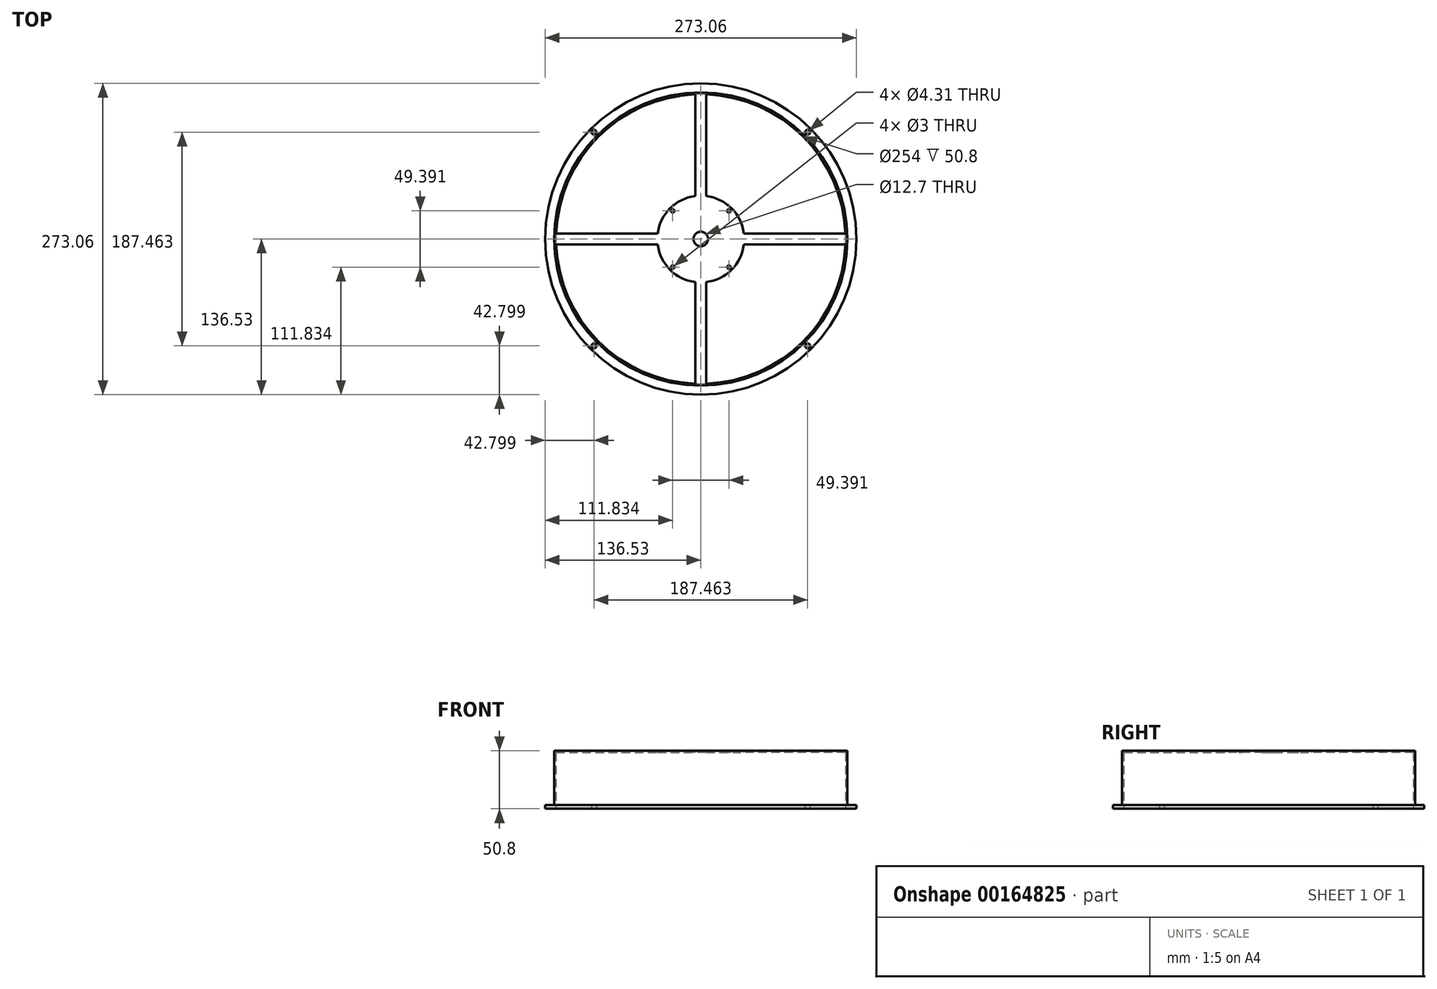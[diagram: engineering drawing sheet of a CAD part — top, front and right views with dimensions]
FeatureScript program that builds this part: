
annotation { "Feature Type Name" : "Feature", "Feature Type Description" : "" }
export const myFeature = defineFeature(function(context is Context, id is Id, definition is map)
    precondition{}
    {
        {
            var Q0;
            Q0=qCreatedBy(makeId("Top.planeOp"),FACE);
            var sketch = newSketch(context, id + "F0", { "sketchPlane" : qUnion([Q0])});
            skCircle(sketch, "E0", {"center": v(0, 0) * mm, "radius": 136.53 * mm});
            skLineSegment(sketch, "E1.bottom", {"start": v(93.73, 93.73) * mm, "end": v(-93.73, 93.73) * mm, "construction": true});
            skLineSegment(sketch, "E1.top", {"start": v(93.73, -93.73) * mm, "end": v(-93.73, -93.73) * mm, "construction": true});
            skLineSegment(sketch, "E1.left", {"start": v(93.73, 93.73) * mm, "end": v(93.73, -93.73) * mm, "construction": true});
            skLineSegment(sketch, "E1.right", {"start": v(-93.73, 93.73) * mm, "end": v(-93.73, -93.73) * mm, "construction": true});
            skCircle(sketch, "E2", {"center": v(93.73, 93.73) * mm, "radius": 3.97 * mm, "construction": true});
            skCircle(sketch, "E3", {"center": v(-93.73, 93.73) * mm, "radius": 2.15 * mm});
            skCircle(sketch, "E4", {"center": v(93.73, 93.73) * mm, "radius": 2.15 * mm});
            skCircle(sketch, "E5", {"center": v(93.73, -93.73) * mm, "radius": 2.15 * mm});
            skCircle(sketch, "E6", {"center": v(-93.73, -93.73) * mm, "radius": 2.15 * mm});
            skCircle(sketch, "E7", {"center": v(0, 0) * mm, "radius": 127 * mm});
            skSolve(sketch);
        }
        {
            var Q0;
            Q0 = qSketchRegion(id + "F0", true);
            extrude(context, id + "F1", {"entities" : qUnion([Q0]), "depth" : 3.17 * mm});
        }
        {
            var Q0;
            Q0=makeQuery(id+"F1.opExtrude","CAP_FACE",FACE,{"disambiguationData":[OSD([sQuery(id+"F0.wireOp",EDGE,"E0"),sQuery(id+"F0.wireOp",EDGE,"E3"),sQuery(id+"F0.wireOp",EDGE,"E4"),sQuery(id+"F0.wireOp",EDGE,"E5"),sQuery(id+"F0.wireOp",EDGE,"E6"),sQuery(id+"F0.wireOp",EDGE,"E7")])],"isStart":false});
            var sketch = newSketch(context, id + "F2", { "sketchPlane" : qUnion([Q0])});
            skCircle(sketch, "E8", {"center": v(0, 0) * mm, "radius": 127 * mm});
            skCircle(sketch, "E9", {"center": v(0, 0) * mm, "radius": 128.59 * mm});
            skSolve(sketch);
        }
        {
            var Q0;
            Q0 = qSketchRegion(id + "F2", true);
            extrude(context, id + "F3", {"entities" : qUnion([Q0]), "operationType" : NewBodyOperationType.ADD, "depth" : 47.62 * mm});
        }
        {
            var Q0;
            Q0=makeQuery(id+"F3.opExtrude","CAP_FACE",FACE,{"disambiguationData":[OSD([sQuery(id+"F2.wireOp",EDGE,"E8"),sQuery(id+"F2.wireOp",EDGE,"E9")])],"isStart":false});
            var sketch = newSketch(context, id + "F4", { "sketchPlane" : qUnion([Q0])});
            skLineSegment(sketch, "E10.bottom", {"start": v(-126.91, 4.76) * mm, "end": v(-37.8, 4.76) * mm});
            skLineSegment(sketch, "E10.top", {"start": v(-126.91, -4.76) * mm, "end": v(-37.8, -4.76) * mm});
            skLineSegment(sketch, "E10.left", {"start": v(-126.91, 4.76) * mm, "end": v(-126.91, -4.76) * mm, "construction": true});
            skLineSegment(sketch, "E10.right", {"start": v(-37.8, 4.76) * mm, "end": v(-37.8, -4.76) * mm});
            skLineSegment(sketch, "E11.bottom", {"start": v(126.91, -4.76) * mm, "end": v(37.8, -4.76) * mm});
            skLineSegment(sketch, "E11.top", {"start": v(126.91, 4.76) * mm, "end": v(37.8, 4.76) * mm});
            skLineSegment(sketch, "E11.left", {"start": v(126.91, -4.76) * mm, "end": v(126.91, 4.76) * mm, "construction": true});
            skLineSegment(sketch, "E11.right", {"start": v(37.8, -4.76) * mm, "end": v(37.8, 4.76) * mm});
            skLineSegment(sketch, "E12.bottom", {"start": v(-4.76, -126.91) * mm, "end": v(4.76, -126.91) * mm, "construction": true});
            skLineSegment(sketch, "E12.top", {"start": v(-4.76, -37.8) * mm, "end": v(4.76, -37.8) * mm});
            skLineSegment(sketch, "E12.left", {"start": v(-4.76, -126.91) * mm, "end": v(-4.76, -37.8) * mm});
            skLineSegment(sketch, "E12.right", {"start": v(4.76, -126.91) * mm, "end": v(4.76, -37.8) * mm});
            skLineSegment(sketch, "E13.bottom", {"start": v(-4.76, 126.91) * mm, "end": v(4.76, 126.91) * mm, "construction": true});
            skLineSegment(sketch, "E13.top", {"start": v(-4.76, 37.8) * mm, "end": v(4.76, 37.8) * mm});
            skLineSegment(sketch, "E13.left", {"start": v(-4.76, 126.91) * mm, "end": v(-4.76, 37.8) * mm});
            skLineSegment(sketch, "E13.right", {"start": v(4.76, 126.91) * mm, "end": v(4.76, 37.8) * mm});
            skLineSegment(sketch, "E14", {"start": v(0, 37.8) * mm, "end": v(0, -37.8) * mm, "construction": true});
            skArc(sketch, "E15", {"start": v(-37.8, -4.76) * mm, "mid": v(-26.94, -26.94) * mm, "end": v(-4.76, -37.8) * mm});
            skLineSegment(sketch, "E16", {"start": v(-37.8, 0) * mm, "end": v(37.8, 0) * mm, "construction": true});
            skArc(sketch, "E17", {"start": v(-4.76, 37.8) * mm, "mid": v(-26.94, 26.94) * mm, "end": v(-37.8, 4.76) * mm});
            skArc(sketch, "E18", {"start": v(37.8, 4.76) * mm, "mid": v(26.94, 26.94) * mm, "end": v(4.76, 37.8) * mm});
            skArc(sketch, "E19", {"start": v(4.76, -37.8) * mm, "mid": v(26.94, -26.94) * mm, "end": v(37.8, -4.76) * mm});
            skArc(sketch, "E20", {"start": v(4.76, 126.91) * mm, "mid": v(0, 127) * mm, "end": v(-4.76, 126.91) * mm});
            skCircle(sketch, "E21", {"center": v(0, 0) * mm, "radius": 127 * mm});
            skSolve(sketch);
        }
        {
            var Q0;
            {var subQ0=sQuery(id+"F4.wireOp",EDGE,"E10.bottom");Q0=makeQuery(id+"F4.imprint","IMPRINT",FACE,{"disambiguationData":[TD([[makeQuery(id+"F4.imprint","IMPRINT",EDGE,{"derivedFrom":subQ0}),-1.0]])]});}
            var Q1;
            {var subQ0=sQuery(id+"F4.wireOp",EDGE,"E11.bottom");Q1=makeQuery(id+"F4.imprint","IMPRINT",FACE,{"disambiguationData":[TD([[makeQuery(id+"F4.imprint","IMPRINT",EDGE,{"derivedFrom":subQ0}),-1.0]])]});}
            var Q2;
            Q2=makeQuery(id+"F4.imprint","IMPRINT",FACE,{"disambiguationData":[TD([[makeQuery(id+"F4.imprint","IMPRINT",EDGE,{"derivedFrom":sQuery(id+"F4.wireOp",EDGE,"E12.top")}),-1.0]])]});
            var Q3;
            Q3=makeQuery(id+"F4.imprint","IMPRINT",FACE,{"disambiguationData":[TD([[makeQuery(id+"F4.imprint","IMPRINT",EDGE,{"derivedFrom":sQuery(id+"F4.wireOp",EDGE,"E13.top")}),1.0]])]});
            var Q4;
            Q4=makeQuery(id+"F4.imprint","IMPRINT",FACE,{"disambiguationData":[TD([[makeQuery(id+"F4.imprint","IMPRINT",EDGE,{"derivedFrom":sQuery(id+"F4.wireOp",EDGE,"E10.right")}),1.0]])]});
            extrude(context, id + "F5", {"entities" : qUnion([Q0, Q1, Q2, Q3, Q4]), "operationType" : NewBodyOperationType.ADD, "oppositeDirection" : true, "depth" : 1.59 * mm});
        }
        {
            var Q0;
            Q0=makeQuery(id+"F5.boolean.opBoolean","MERGE",FACE,{"derivedFrom":[makeQuery(id+"F3.opExtrude","CAP_FACE",FACE,{"disambiguationData":[OSD([sQuery(id+"F2.wireOp",EDGE,"E8"),sQuery(id+"F2.wireOp",EDGE,"E9")])],"isStart":false}),makeQuery(id+"F5.opExtrude","CAP_FACE",FACE,{"disambiguationData":[OSD([sQuery(id+"F4.wireOp",EDGE,"E10.bottom"),sQuery(id+"F4.wireOp",EDGE,"E10.top"),sQuery(id+"F4.wireOp",EDGE,"E11.bottom"),sQuery(id+"F4.wireOp",EDGE,"E11.top"),sQuery(id+"F4.wireOp",EDGE,"E12.left"),sQuery(id+"F4.wireOp",EDGE,"E12.right"),sQuery(id+"F4.wireOp",EDGE,"E13.left"),sQuery(id+"F4.wireOp",EDGE,"E13.right"),sQuery(id+"F4.wireOp",EDGE,"E15"),sQuery(id+"F4.wireOp",EDGE,"E17"),sQuery(id+"F4.wireOp",EDGE,"E18"),sQuery(id+"F4.wireOp",EDGE,"E19"),sQuery(id+"F4.wireOp",EDGE,"E21")])],"isStart":true})]});
            var sketch = newSketch(context, id + "F6", { "sketchPlane" : qUnion([Q0])});
            skLineSegment(sketch, "E22.bottom", {"start": v(24.7, 24.7) * mm, "end": v(-24.7, 24.7) * mm, "construction": true});
            skLineSegment(sketch, "E22.top", {"start": v(24.7, -24.7) * mm, "end": v(-24.7, -24.7) * mm, "construction": true});
            skLineSegment(sketch, "E22.left", {"start": v(24.7, 24.7) * mm, "end": v(24.7, -24.7) * mm, "construction": true});
            skLineSegment(sketch, "E22.right", {"start": v(-24.7, 24.7) * mm, "end": v(-24.7, -24.7) * mm, "construction": true});
            skPoint(sketch, "E22.middle", {"position": v(0, 0) * mm});
            skCircle(sketch, "E23", {"center": v(24.7, 24.7) * mm, "radius": 3.17 * mm, "construction": true});
            skCircle(sketch, "E24", {"center": v(24.7, 24.7) * mm, "radius": 1.5 * mm});
            skCircle(sketch, "E25", {"center": v(24.7, -24.7) * mm, "radius": 1.5 * mm});
            skCircle(sketch, "E26", {"center": v(-24.7, -24.7) * mm, "radius": 1.5 * mm});
            skCircle(sketch, "E27", {"center": v(-24.7, 24.7) * mm, "radius": 1.5 * mm});
            skCircle(sketch, "E28", {"center": v(0, 0) * mm, "radius": 6.35 * mm});
            skSolve(sketch);
        }
        {
            var Q0;
            Q0 = qSketchRegion(id + "F6", true);
            var Q1;
            Q1=makeQuery(id+"F5.opExtrude","CAP_FACE",FACE,{"disambiguationData":[OSD([sQuery(id+"F4.wireOp",EDGE,"E10.bottom"),sQuery(id+"F4.wireOp",EDGE,"E10.top"),sQuery(id+"F4.wireOp",EDGE,"E11.bottom"),sQuery(id+"F4.wireOp",EDGE,"E11.top"),sQuery(id+"F4.wireOp",EDGE,"E12.left"),sQuery(id+"F4.wireOp",EDGE,"E12.right"),sQuery(id+"F4.wireOp",EDGE,"E13.left"),sQuery(id+"F4.wireOp",EDGE,"E13.right"),sQuery(id+"F4.wireOp",EDGE,"E15"),sQuery(id+"F4.wireOp",EDGE,"E17"),sQuery(id+"F4.wireOp",EDGE,"E18"),sQuery(id+"F4.wireOp",EDGE,"E19"),sQuery(id+"F4.wireOp",EDGE,"E21")])],"isStart":false});
            extrude(context, id + "F7", {"entities" : qUnion([Q0]), "operationType" : NewBodyOperationType.REMOVE, "endBound" : BoundingType.UP_TO_SURFACE, "oppositeDirection" : true, "endBoundEntityFace" : qUnion([Q1]), "depth" : 25.4 * mm});
        }
    });
